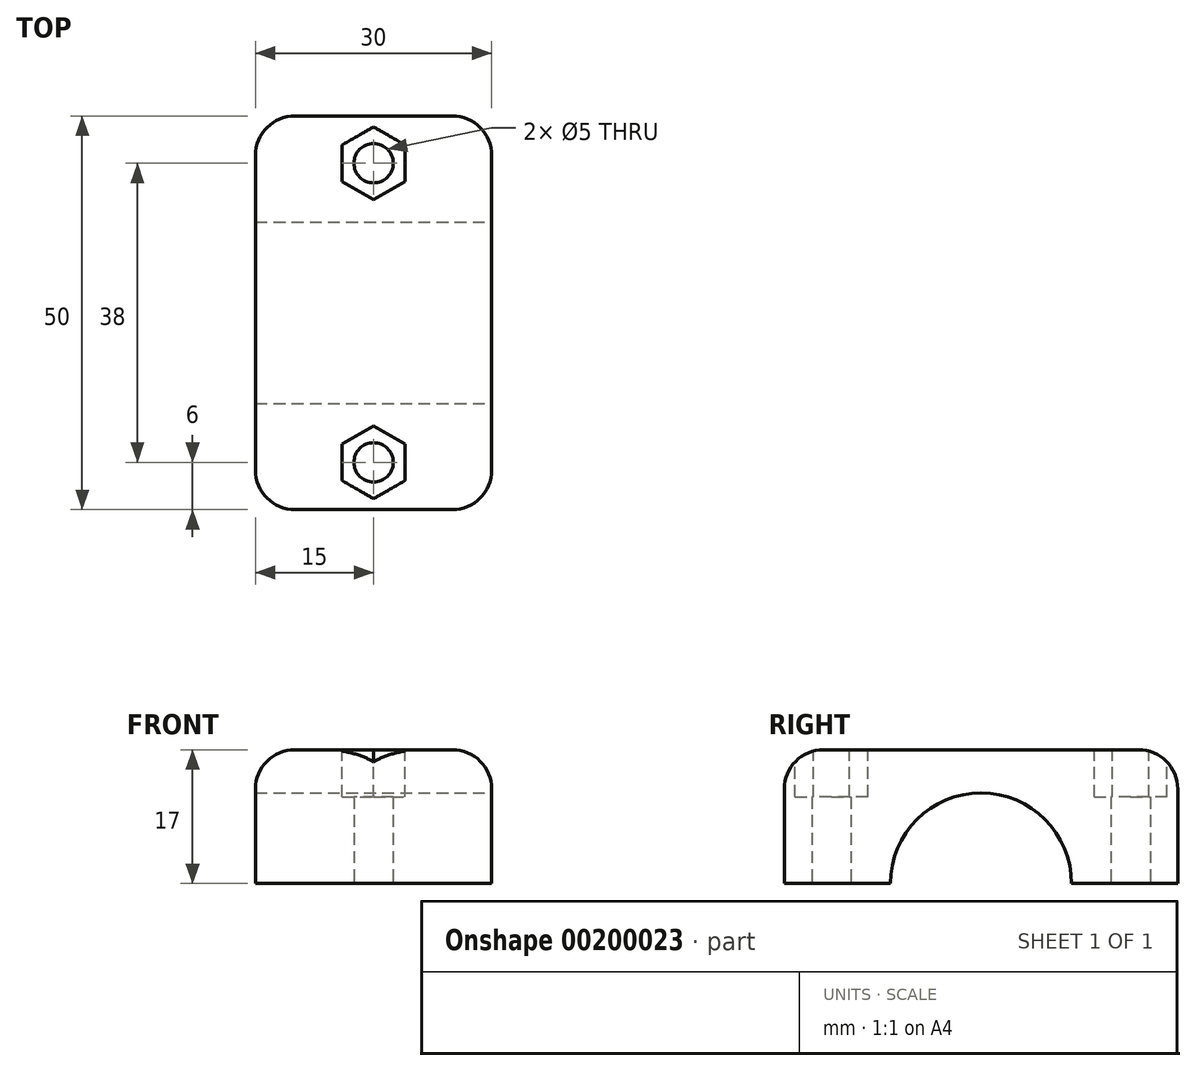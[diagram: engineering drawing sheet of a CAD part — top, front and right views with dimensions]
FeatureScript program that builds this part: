
annotation { "Feature Type Name" : "Feature", "Feature Type Description" : "" }
export const myFeature = defineFeature(function(context is Context, id is Id, definition is map)
    precondition{}
    {
        {
            var Q0;
            Q0=qCreatedBy(makeId("Top.planeOp"),FACE);
            var sketch = newSketch(context, id + "F0", { "sketchPlane" : qUnion([Q0])});
            skPoint(sketch, "E0", {"position": v(-15, 0) * mm});
            skPoint(sketch, "E1", {"position": v(15, 0) * mm});
            skPoint(sketch, "E2", {"position": v(0, 25) * mm});
            skPoint(sketch, "E3", {"position": v(0, -25) * mm});
            skPoint(sketch, "E4", {"position": v(0, 0) * mm});
            skPoint(sketch, "E5", {"position": v(0, 19) * mm});
            skPoint(sketch, "E6", {"position": v(0, -19) * mm});
            skLineSegment(sketch, "E7.bottom", {"start": v(-15, -25) * mm, "end": v(15, -25) * mm});
            skLineSegment(sketch, "E7.top", {"start": v(-15, 25) * mm, "end": v(15, 25) * mm});
            skLineSegment(sketch, "E7.left", {"start": v(-15, -25) * mm, "end": v(-15, 25) * mm});
            skLineSegment(sketch, "E7.right", {"start": v(15, -25) * mm, "end": v(15, 25) * mm});
            skLineSegment(sketch, "E8", {"start": v(-15, 0) * mm, "end": v(15, 0) * mm});
            skSolve(sketch);
        }
        {
            var Q0;
            {var subQ0=sQuery(id+"F0.wireOp",EDGE,"E7.top");Q0=makeQuery(id+"F0.imprint","IMPRINT",FACE,{"disambiguationData":[TD([[makeQuery(id+"F0.imprint","IMPRINT",EDGE,{"derivedFrom":subQ0}),-1.0]])]});}
            var Q1;
            {var subQ0=sQuery(id+"F0.wireOp",EDGE,"E7.bottom");Q1=makeQuery(id+"F0.imprint","IMPRINT",FACE,{"disambiguationData":[TD([[makeQuery(id+"F0.imprint","IMPRINT",EDGE,{"derivedFrom":subQ0}),1.0]])]});}
            extrude(context, id + "F1", {"entities" : qUnion([Q0, Q1]), "depth" : 17 * mm});
        }
        {
            var Q0;
            Q0=makeQuery(id+"F1.opExtrude","SWEPT_FACE",FACE,{"disambiguationData":[OSD([sQuery(id+"F0.wireOp",EDGE,"E7.right")])]});
            var sketch = newSketch(context, id + "F2", { "sketchPlane" : qUnion([Q0])});
            skCircle(sketch, "E9", {"center": v(0, 0) * mm, "radius": 11.5 * mm});
            skSolve(sketch);
        }
        {
            var Q0;
            {var subQ0=sQuery(id+"F2.wireOp",EDGE,"E9");var subQ1=makeQuery(id+"F1.opExtrude","CAP_EDGE",EDGE,{"disambiguationData":[OSD([sQuery(id+"F0.wireOp",EDGE,"E7.right")])],"isStart":true});var subQ2=makeQuery(id+"F2.imprint","INTERSECT",VERTEX,{"disambiguationData":[OD(0.0)],"derivedFrom":[subQ1,subQ0]});Q0=makeQuery(id+"F2.imprint","IMPRINT",FACE,{"disambiguationData":[TD([[makeQuery(id+"F2.imprint","IMPRINT",EDGE,{"disambiguationData":[TD([[subQ2,1.0]])],"derivedFrom":subQ0}),1.0]])]});}
            var Q1;
            {var subQ0=sQuery(id+"F2.wireOp",EDGE,"E9");var subQ1=makeQuery(id+"F1.opExtrude","CAP_EDGE",EDGE,{"disambiguationData":[OSD([sQuery(id+"F0.wireOp",EDGE,"E7.right")])],"isStart":true});var subQ2=makeQuery(id+"F2.imprint","INTERSECT",VERTEX,{"disambiguationData":[OD(0.0)],"derivedFrom":[subQ1,subQ0]});Q1=makeQuery(id+"F2.imprint","IMPRINT",FACE,{"disambiguationData":[TD([[makeQuery(id+"F2.imprint","IMPRINT",EDGE,{"disambiguationData":[TD([[subQ2,-1.0]])],"derivedFrom":subQ0}),1.0]])]});}
            extrude(context, id + "F3", {"entities" : qUnion([Q0, Q1]), "operationType" : NewBodyOperationType.REMOVE, "oppositeDirection" : true, "depth" : 50 * mm});
        }
        {
            var Q0;
            Q0=sQuery(id+"F0.wireOp",VERTEX,"E5");
            var Q1;
            Q1=sQuery(id+"F0.wireOp",VERTEX,"E6");
            var Q2;
            Q2=makeQuery(id+"F1.opExtrude","SWEPT_BODY",BODY,{"disambiguationData":[OSD([sQuery(id+"F0.wireOp",EDGE,"E7.bottom"),sQuery(id+"F0.wireOp",EDGE,"E7.top"),sQuery(id+"F0.wireOp",EDGE,"E7.left"),sQuery(id+"F0.wireOp",EDGE,"E7.right")])]});
            hole(context, id + "F4", {"style" : HoleStyle.SIMPLE, "endStyle" : HoleEndStyle.THROUGH, "oppositeDirection" : true, "holeDiameter" : 5 * mm, "locations" : qUnion([Q0, Q1]), "scope" : qUnion([Q2]), "isTappedThrough" : true});
        }
        {
            var Q0;
            Q0=makeQuery(id+"F1.opExtrude","CAP_FACE",FACE,{"disambiguationData":[OSD([sQuery(id+"F0.wireOp",EDGE,"E7.bottom"),sQuery(id+"F0.wireOp",EDGE,"E7.top"),sQuery(id+"F0.wireOp",EDGE,"E7.left"),sQuery(id+"F0.wireOp",EDGE,"E7.right")])],"isStart":false});
            var sketch = newSketch(context, id + "F5", { "sketchPlane" : qUnion([Q0])});
            skCircle(sketch, "E10.cCircle", {"center": v(0, 19) * mm, "radius": 4 * mm, "construction": true});
            skLineSegment(sketch, "E10.0", {"start": v(4, 21.3) * mm, "end": v(4, 16.7) * mm});
            skLineSegment(sketch, "E10.1", {"start": v(4, 16.7) * mm, "end": v(0, 14.38) * mm});
            skLineSegment(sketch, "E10.2", {"start": v(0, 14.38) * mm, "end": v(-4, 16.7) * mm});
            skLineSegment(sketch, "E10.3", {"start": v(-4, 16.7) * mm, "end": v(-4, 21.3) * mm});
            skLineSegment(sketch, "E10.4", {"start": v(-4, 21.3) * mm, "end": v(0, 23.62) * mm});
            skLineSegment(sketch, "E10.5", {"start": v(0, 23.62) * mm, "end": v(4, 21.3) * mm});
            skPoint(sketch, "E10.0.midPoint", {"position": v(4, 19) * mm});
            skCircle(sketch, "E11.cCircle", {"center": v(0, -19) * mm, "radius": 4 * mm, "construction": true});
            skLineSegment(sketch, "E11.0", {"start": v(4, -16.7) * mm, "end": v(4, -21.3) * mm});
            skLineSegment(sketch, "E11.1", {"start": v(4, -21.3) * mm, "end": v(0, -23.62) * mm});
            skLineSegment(sketch, "E11.2", {"start": v(0, -23.62) * mm, "end": v(-4, -21.3) * mm});
            skLineSegment(sketch, "E11.3", {"start": v(-4, -21.3) * mm, "end": v(-4, -16.7) * mm});
            skLineSegment(sketch, "E11.4", {"start": v(-4, -16.7) * mm, "end": v(0, -14.38) * mm});
            skLineSegment(sketch, "E11.5", {"start": v(0, -14.38) * mm, "end": v(4, -16.7) * mm});
            skPoint(sketch, "E11.0.midPoint", {"position": v(4, -19) * mm});
            skSolve(sketch);
        }
        {
            var Q0;
            Q0=makeQuery(id+"F5.imprint","IMPRINT",FACE,{"disambiguationData":[TD([[makeQuery(id+"F5.imprint","IMPRINT",EDGE,{"derivedFrom":sQuery(id+"F5.wireOp",EDGE,"E11.0")}),-1.0]])]});
            var Q1;
            Q1=makeQuery(id+"F5.imprint","IMPRINT",FACE,{"disambiguationData":[TD([[makeQuery(id+"F5.imprint","IMPRINT",EDGE,{"derivedFrom":sQuery(id+"F5.wireOp",EDGE,"E10.0")}),-1.0]])]});
            extrude(context, id + "F6", {"entities" : qUnion([Q0, Q1]), "operationType" : NewBodyOperationType.REMOVE, "oppositeDirection" : true, "depth" : 6 * mm});
        }
        {
            var Q0;
            Q0=makeQuery(id+"F1.opExtrude","SWEPT_EDGE",EDGE,{"disambiguationData":[OSD([sQuery(id+"F0.wireOp",EDGE,"E7.top"),sQuery(id+"F0.wireOp",EDGE,"E7.left")])]});
            var Q1;
            Q1=makeQuery(id+"F1.opExtrude","SWEPT_EDGE",EDGE,{"disambiguationData":[OSD([sQuery(id+"F0.wireOp",EDGE,"E7.top"),sQuery(id+"F0.wireOp",EDGE,"E7.right")])]});
            var Q2;
            Q2=makeQuery(id+"F1.opExtrude","SWEPT_EDGE",EDGE,{"disambiguationData":[OSD([sQuery(id+"F0.wireOp",EDGE,"E7.bottom"),sQuery(id+"F0.wireOp",EDGE,"E7.left")])]});
            var Q3;
            Q3=makeQuery(id+"F1.opExtrude","SWEPT_EDGE",EDGE,{"disambiguationData":[OSD([sQuery(id+"F0.wireOp",EDGE,"E7.bottom"),sQuery(id+"F0.wireOp",EDGE,"E7.right")])]});
            fillet(context, id + "F7", {"entities" : qUnion([Q0, Q1, Q2, Q3]), "radius" : 5 * mm, "tangentPropagation" : true, "allowEdgeOverflow" : false});
        }
        {
            var Q0;
            Q0=makeQuery(id+"F1.opExtrude","CAP_EDGE",EDGE,{"disambiguationData":[OSD([sQuery(id+"F0.wireOp",EDGE,"E7.left")])],"isStart":false});
            fillet(context, id + "F8", {"entities" : qUnion([Q0]), "radius" : 5 * mm, "tangentPropagation" : true, "allowEdgeOverflow" : false});
        }
    });
